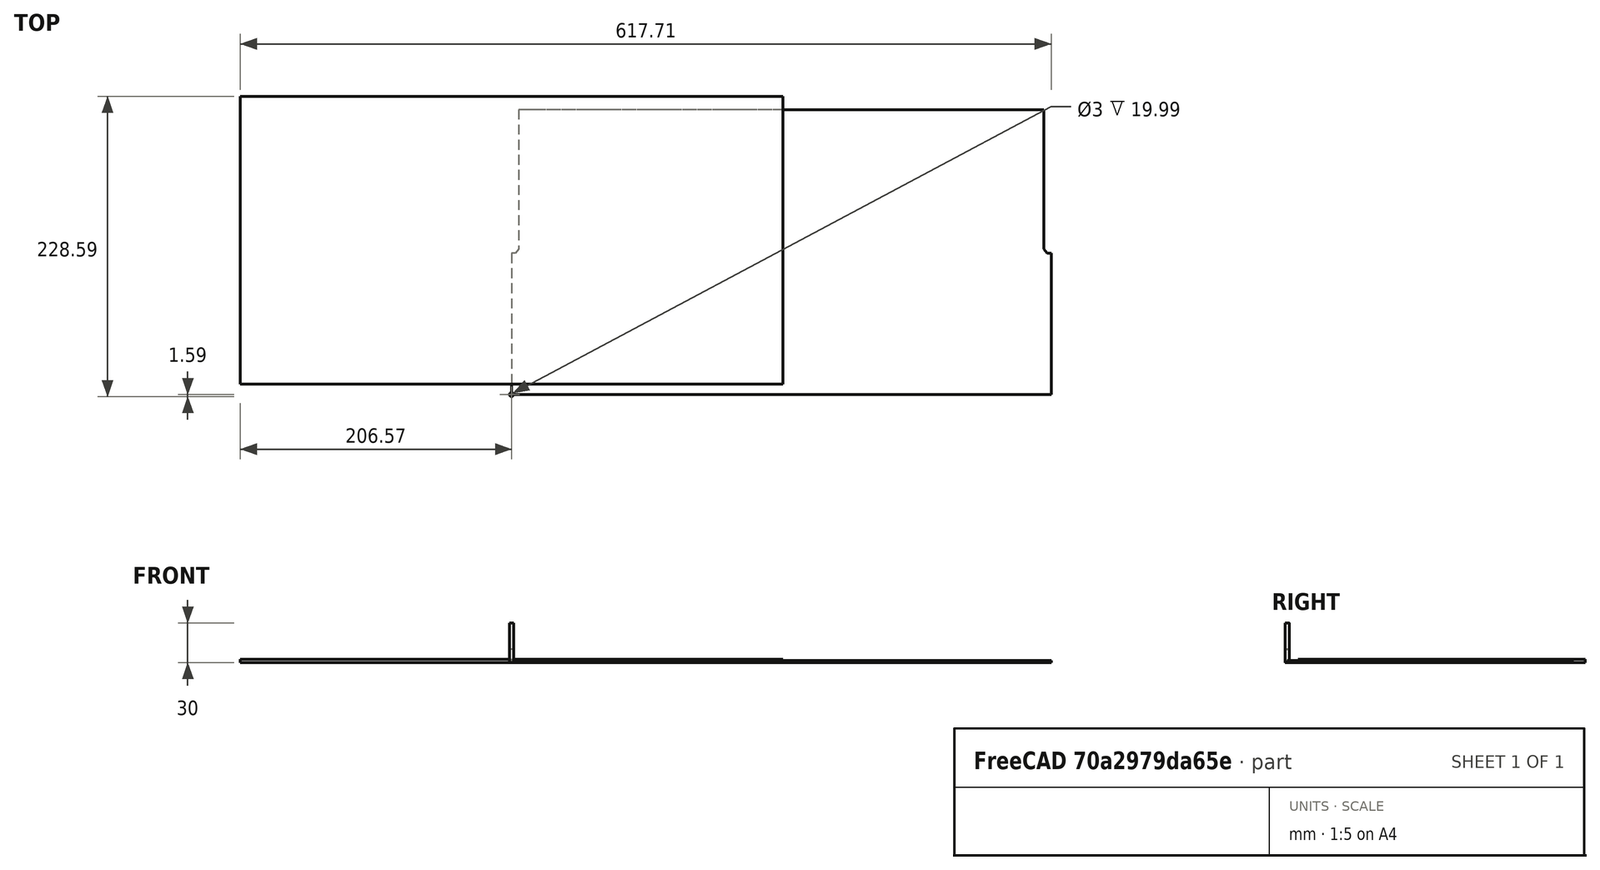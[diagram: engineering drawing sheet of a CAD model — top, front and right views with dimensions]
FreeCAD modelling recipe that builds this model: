
FCSTD DOCUMENT  (FreeCAD 0.22R37100 (Git))
Label: composit_stand10_plexiglass_cut
License: All rights reserved
LicenseURL: http://en.wikipedia.org/wiki/All_rights_reserved
objects: App::DocumentObjectGroup×4, Path::FeaturePython×4, Part::FeaturePython×3, App::Link×1, App::FeaturePython×1, Measure::MeasureDistance×1, Measure::MeasureLength×1
note: 4 computed .brp shape members not serialized (recipe doc carries the construction recipe); baked Part::Feature solids carry a one-line shape summary decoded from their .brp
EXTERNAL_REF file=composit_stand10.FCStd obj=Body024

FEATURE [App::Link] Link  label="Body024"
  LinkedObject = -> <external composit_stand10.FCStd>#Body024
  expr: LinkedObject = composit_stand10#<<Body024>>._self
FEATURE [App::FeaturePython] SetupSheet  # Path/CAM operation (typed FeaturePython)
  ClearanceHeightExpression = OpStockZMax+SetupSheet.ClearanceHeightOffset
  ClearanceHeightOffset = 5
  CoolantMode = 0
  CoolantModes = None | Flood | Mist
  FinalDepthExpression = OpFinalDepth
  HorizRapid = 0
  ProfileDirection = 1
  ProfileprocessCircles = true
  ProfileprocessHoles = true
  ProfileprocessPerimeter = true
  SafeHeightExpression = OpStockZMax+SetupSheet.SafeHeightOffset
  SafeHeightOffset = 3
  StartDepthExpression = OpStartDepth
  StepDownExpression = OpToolDiameter
  VertRapid = 0
FEATURE [Part::FeaturePython] Clone  label="Model-Body024"  # Draft clone (typed FeaturePython)
  AttacherType = Attacher::AttachEngine3D
  Fuse = false
  Objects = -> [Link]
  PathResource = Model
  Placement = pos=(205.571,-9,0) rot=(0,0,1;0rad)
  Scale = (1,1,1)
FEATURE [App::DocumentObjectGroup] Model
  Group = -> [Clone]
FEATURE [Part::FeaturePython] ToolBit  label="3.175mm Endmill"  # Path/CAM toolbit (typed FeaturePython)
  BitPropertyNames = Chipload | CuttingEdgeHeight | Diameter | Flutes | Length | Material | ShankDiameter | SpindleDirection
  BitShape = <path>
  Chipload = 0
  CuttingEdgeHeight = 30
  Diameter = 3.175
  Flutes = 0
  Length = 10
  Material = 0
  ShankDiameter = 3
  ShapeName = endmill
  SpindleDirection = 0
FEATURE [Path::FeaturePython] __175mm_Endmill  label="3.175mm Endmill001"  # Path/CAM operation (typed FeaturePython)
  HorizFeed = 51.6667
  HorizRapid = 0
  SpindleDir = 0
  SpindleSpeed = 18000
  Tool = -> ToolBit
  ToolNumber = 1
  VertFeed = 35
  VertRapid = 0
  expr: HorizRapid = SetupSheet.HorizRapid
  expr: VertRapid = SetupSheet.VertRapid
FEATURE [App::DocumentObjectGroup] Tools
  Group = -> [__175mm_Endmill]
FEATURE [Part::FeaturePython] Stock  # WARN: FeaturePython — macro-defined, semantics opaque (R4)
  Base = -> Model
  ExtXneg = 1
  ExtXpos = 1
  ExtYneg = 1
  ExtYpos = 1
  ExtZneg = 0
  ExtZpos = 1
  Placement = pos=(-205.571,9,0) rot=(0,0,1;0rad)
  StockType = FromBase
FEATURE [Path::FeaturePython] Profile  # Path/CAM operation (typed FeaturePython)
  Active = true
  AreaParams:
    Tolerance = 1e-07
    FitArcs = True
    Simplify = False
    CleanDistance = 0.0
    Accuracy = 0.01
    Unit = 1.0
    MinArcPoints = 4
    MaxArcPoints = 100
    ClipperScale = 10000000.0
    Fill = 0
    Coplanar = 0
    Reorient = True
    Outline = False
    Explode = False
    OpenMode = 0
    Deflection = 0.01
    SubjectFill = 0
    ClipFill = 0
    Offset = 1.5875
    ExtraPass = 0
    Stepover = 0.0
    LastStepover = 0.0
    JoinType = 0
    EndType = 0
    MiterLimit = 2.0
    RoundPrecision = 0.0
    PocketMode = 0
    ToolRadius = 1.0
    PocketExtraOffset = 0.0
    PocketStepover = 0.0
    PocketLastStepover = 0.0
    FromCenter = False
    Angle = 45.0
    AngleShift = 0.0
    Shift = 0.0
    Thicken = False
    SectionCount = -1
    Stepdown = 1.0
    SectionOffset = 0.0
    SectionTolerance = 1e-06
    SectionMode = 2
    Project = False
  ClearanceHeight = 7.5
  CoolantMode = 0
  CycleTime = 00:00:29
  Direction = 1
  FinalDepth = 0
  HandleMultipleFeatures = 0
  JoinType = 0
  MiterLimit = 0.1
  OffsetExtra = 0
  OpFinalDepth = 0
  OpStartDepth = 2.5
  OpStockZMax = 2.5
  OpStockZMin = 0
  OpToolDiameter = 3.175
  PathParams = {'orientation': 0, 'feedrate': 51.666666666666664, 'feedrate_v': 35.0, 'verbose': True, 'resume_height': 5.5, 'retraction': 7.5, 'return_end': True, 'preamble': False, 'start': Vector (0.0, 217.0, 0.0)}
  SafeHeight = 5.5
  Side = 0
  SplitArcs = false
  StartDepth = 2.5
  StartPoint = (0,217,0)
  StepDown = 3.175
  ToolController = -> __175mm_Endmill
  UseComp = true
  UseStartPoint = true
  processCircles = true
  processHoles = true
  processPerimeter = true
  expr: ClearanceHeight = OpStockZMax + SetupSheet.ClearanceHeightOffset
  expr: FinalDepth = OpFinalDepth
  expr: SafeHeight = OpStockZMax + SetupSheet.SafeHeightOffset
  expr: StartDepth = OpStartDepth
  expr: StepDown = OpToolDiameter
FEATURE [Measure::MeasureDistance] Distance
  Distance = 217
  Element1 = -> Clone [Edge30]
  Element2 = -> Clone [Edge29]
  Position1 = (405.571,0,1.5)
  Position2 = (405.571,217,1.5)
FEATURE [Measure::MeasureLength] Length
  Elements = -> [Clone]
  Length = 411.142
FEATURE [App::DocumentObjectGroup] Measurements
  Group = -> [Distance,Length]
FEATURE [Path::FeaturePython] Array  # Path/CAM operation (typed FeaturePython)
  Active = true
  Angle = 0
  Base = -> [Profile]
  Centre = (0,0,0)
  Copies = 2
  CopiesX = 0
  CopiesY = 0
  JitterMagnitude = (0,0,0)
  JitterPercent = 0
  JitterSeed = 0
  Offset = (414.35,0,0)
  SwapDirection = false
  ToolController = -> __175mm_Endmill
  Type = 0
FEATURE [App::DocumentObjectGroup] Operations
  Group = -> [Profile,Array]
FEATURE [Path::FeaturePython] Job  label="1-1-10-plexiglass_cut"  # Path/CAM operation (typed FeaturePython)
  CycleTime = 00:00:29
  Fixtures = G54
  GeometryTolerance = 0.01
  JobType = 0
  LastPostProcessDate = 2024-07-31 13:06:08.980807
  LastPostProcessOutput = <path>
  Model = -> Model
  Operations = -> Operations
  OrderOutputBy = 2
  PostProcessor = 13
  PostProcessorOutputFile = <path>/%j.tap
  SetupSheet = -> SetupSheet
  SplitOutput = false
  Stock = -> Stock
  Tools = -> Tools
note: 3 file-system paths scrubbed to <path> (originals preserved in the JSON sidecar)
